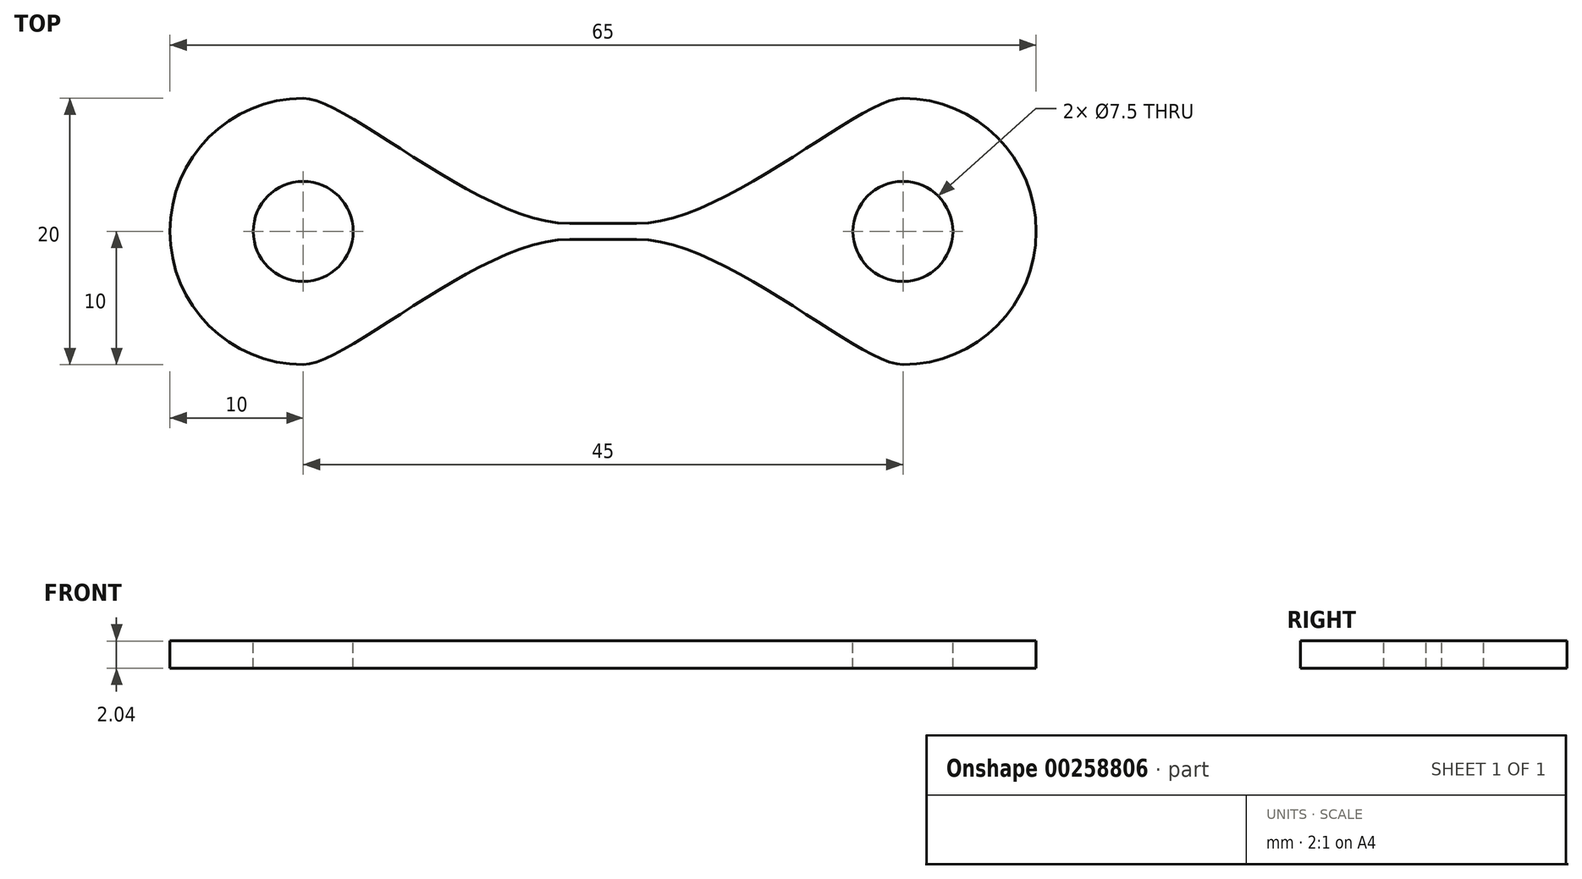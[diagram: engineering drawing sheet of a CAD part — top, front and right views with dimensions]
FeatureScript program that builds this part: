
annotation { "Feature Type Name" : "Feature", "Feature Type Description" : "" }
export const myFeature = defineFeature(function(context is Context, id is Id, definition is map)
    precondition{}
    {
        {
            var Q0;
            Q0=qCreatedBy(makeId("Right.planeOp"),FACE);
            var sketch = newSketch(context, id + "F0", { "sketchPlane" : qUnion([Q0])});
            skLineSegment(sketch, "E0.bottom", {"start": v(0.59, -1.02) * mm, "end": v(-0.59, -1.02) * mm});
            skLineSegment(sketch, "E0.top", {"start": v(0.59, 1.02) * mm, "end": v(-0.59, 1.02) * mm});
            skLineSegment(sketch, "E0.left", {"start": v(0.59, -1.02) * mm, "end": v(0.59, 1.02) * mm});
            skLineSegment(sketch, "E0.right", {"start": v(-0.59, -1.02) * mm, "end": v(-0.59, 1.02) * mm});
            skPoint(sketch, "E0.middle", {"position": v(0, 0) * mm});
            skSolve(sketch);
        }
        {
            var Q0;
            Q0=makeQuery(id+"F0.imprint","IMPRINT",FACE,{"disambiguationData":[TD([[makeQuery(id+"F0.imprint","IMPRINT",EDGE,{"derivedFrom":sQuery(id+"F0.wireOp",EDGE,"E0.bottom")}),-1.0]])]});
            extrude(context, id + "F1", {"entities" : qUnion([Q0]), "depth" : 2.5 * mm});
        }
        {
            var Q0;
            Q0=makeQuery(id+"F1.opExtrude","CAP_FACE",FACE,{"disambiguationData":[OSD([sQuery(id+"F0.wireOp",EDGE,"E0.bottom"),sQuery(id+"F0.wireOp",EDGE,"E0.top"),sQuery(id+"F0.wireOp",EDGE,"E0.left"),sQuery(id+"F0.wireOp",EDGE,"E0.right")])],"isStart":false});
            cPlane(context, id + "F2", {"entities" : qUnion([Q0]), "cplaneType" : CPlaneType.OFFSET, "offset" : 20 * mm, "width" : 150 * mm, "height" : 150 * mm});
        }
        {
            var Q0;
            Q0=qCreatedBy(id+"F2.planeOp",FACE);
            var sketch = newSketch(context, id + "F3", { "sketchPlane" : qUnion([Q0])});
            skLineSegment(sketch, "E1.bottom", {"start": v(10, -1.02) * mm, "end": v(-10, -1.02) * mm});
            skLineSegment(sketch, "E1.top", {"start": v(10, 1.02) * mm, "end": v(-10, 1.02) * mm});
            skLineSegment(sketch, "E1.left", {"start": v(10, -1.02) * mm, "end": v(10, 1.02) * mm});
            skLineSegment(sketch, "E1.right", {"start": v(-10, -1.02) * mm, "end": v(-10, 1.02) * mm});
            skPoint(sketch, "E1.middle", {"position": v(0, 0) * mm});
            skSolve(sketch);
        }
        {
            var Q1;
            Q1=makeQuery(id+"F1.opExtrude","CAP_FACE",FACE,{"disambiguationData":[OSD([sQuery(id+"F0.wireOp",EDGE,"E0.bottom"),sQuery(id+"F0.wireOp",EDGE,"E0.top"),sQuery(id+"F0.wireOp",EDGE,"E0.left"),sQuery(id+"F0.wireOp",EDGE,"E0.right")])],"isStart":false});
            var Q2;
            Q2=makeQuery(id+"F3.imprint","IMPRINT",FACE,{"disambiguationData":[TD([[makeQuery(id+"F3.imprint","IMPRINT",EDGE,{"derivedFrom":sQuery(id+"F3.wireOp",EDGE,"E1.bottom")}),-1.0]])]});
            loft(context, id + "F4", {"operationType" : NewBodyOperationType.ADD, "startCondition" : LoftEndDerivativeType.NORMAL_TO_PROFILE, "startMagnitude" : 1, "endCondition" : LoftEndDerivativeType.NORMAL_TO_PROFILE, "endMagnitude" : 0.5, "sheetProfilesArray" : [{ "sheetProfileEntities" : qUnion([Q1]) }, { "sheetProfileEntities" : qUnion([Q2]) }]});
        }
        {
            var Q0;
            Q0=qCreatedBy(makeId("Top.planeOp"),FACE);
            var sketch = newSketch(context, id + "F5", { "sketchPlane" : qUnion([Q0])});
            skArc(sketch, "E2", {"start": v(22.5, 10) * mm, "mid": v(32.5, 0) * mm, "end": v(22.5, -10) * mm});
            skLineSegment(sketch, "E3", {"start": v(22.5, 10) * mm, "end": v(22.5, -10) * mm});
            skSolve(sketch);
        }
        {
            var Q0;
            Q0 = qSketchRegion(id + "F5", true);
            var Q1;
            {var subQ0=sQuery(id+"F0.wireOp",EDGE,"E0.top");Q1=makeQuery(id+"F4.boolean.opBoolean","MERGE",FACE,{"derivedFrom":[makeQuery(id+"F1.opExtrude","SWEPT_FACE",FACE,{"disambiguationData":[OSD([subQ0])]}),makeQuery(id+"F4.opLoft","SWEPT_FACE",FACE,{"disambiguationData":[OSD([subQ0,sQuery(id+"F0.wireOp",EDGE,"E0.left"),sQuery(id+"F0.wireOp",EDGE,"E0.right"),sQuery(id+"F3.wireOp",EDGE,"E1.top"),sQuery(id+"F3.wireOp",EDGE,"E1.left"),sQuery(id+"F3.wireOp",EDGE,"E1.right")])]})]});}
            var Q2;
            {var subQ0=sQuery(id+"F0.wireOp",EDGE,"E0.bottom");Q2=makeQuery(id+"F4.boolean.opBoolean","MERGE",FACE,{"derivedFrom":[makeQuery(id+"F1.opExtrude","SWEPT_FACE",FACE,{"disambiguationData":[OSD([subQ0])]}),makeQuery(id+"F4.opLoft","SWEPT_FACE",FACE,{"disambiguationData":[OSD([subQ0,sQuery(id+"F0.wireOp",EDGE,"E0.left"),sQuery(id+"F0.wireOp",EDGE,"E0.right"),sQuery(id+"F3.wireOp",EDGE,"E1.bottom"),sQuery(id+"F3.wireOp",EDGE,"E1.left"),sQuery(id+"F3.wireOp",EDGE,"E1.right")])]})]});}
            extrude(context, id + "F6", {"entities" : qUnion([Q0]), "operationType" : NewBodyOperationType.ADD, "endBound" : BoundingType.UP_TO_SURFACE, "endBoundEntityFace" : qUnion([Q1]), "depth" : 25 * mm, "hasSecondDirection" : true, "secondDirectionBound" : SecondDirectionBoundingType.UP_TO_SURFACE, "secondDirectionOppositeDirection" : true, "secondDirectionBoundEntityFace" : qUnion([Q2]), "secondDirectionDepth" : 25 * mm});
        }
        {
            var Q0;
            {var subQ0=sQuery(id+"F0.wireOp",EDGE,"E0.top");Q0=makeQuery(id+"F6.boolean.opBoolean","MERGE",FACE,{"derivedFrom":[makeQuery(id+"F4.boolean.opBoolean","MERGE",FACE,{"derivedFrom":[makeQuery(id+"F1.opExtrude","SWEPT_FACE",FACE,{"disambiguationData":[OSD([subQ0])]}),makeQuery(id+"F4.opLoft","SWEPT_FACE",FACE,{"disambiguationData":[OSD([subQ0,sQuery(id+"F0.wireOp",EDGE,"E0.left"),sQuery(id+"F0.wireOp",EDGE,"E0.right"),sQuery(id+"F3.wireOp",EDGE,"E1.top"),sQuery(id+"F3.wireOp",EDGE,"E1.left"),sQuery(id+"F3.wireOp",EDGE,"E1.right")])]})]}),makeQuery(id+"F6.opExtrude","CAP_FACE",FACE,{"disambiguationData":[OSD([sQuery(id+"F5.wireOp",EDGE,"E2"),sQuery(id+"F5.wireOp",EDGE,"E3")])],"isStart":false})]});}
            var sketch = newSketch(context, id + "F7", { "sketchPlane" : qUnion([Q0])});
            skCircle(sketch, "E4", {"center": v(22.5, 0) * mm, "radius": 3.75 * mm});
            skSolve(sketch);
        }
        {
            var Q0;
            Q0=makeQuery(id+"F7.imprint","IMPRINT",FACE,{"disambiguationData":[TD([[makeQuery(id+"F7.imprint","IMPRINT",EDGE,{"derivedFrom":sQuery(id+"F7.wireOp",EDGE,"E4")}),1.0]])]});
            extrude(context, id + "F8", {"entities" : qUnion([Q0]), "operationType" : NewBodyOperationType.REMOVE, "endBound" : BoundingType.UP_TO_NEXT, "oppositeDirection" : true, "depth" : 25 * mm});
        }
        {
            var Q0;
            Q0=makeQuery(id+"F1.opExtrude","SWEPT_BODY",BODY,{"disambiguationData":[OSD([sQuery(id+"F0.wireOp",EDGE,"E0.bottom"),sQuery(id+"F0.wireOp",EDGE,"E0.top"),sQuery(id+"F0.wireOp",EDGE,"E0.left"),sQuery(id+"F0.wireOp",EDGE,"E0.right")])]});
            var Q1;
            Q1=makeQuery(id+"F1.opExtrude","CAP_FACE",FACE,{"disambiguationData":[OSD([sQuery(id+"F0.wireOp",EDGE,"E0.bottom"),sQuery(id+"F0.wireOp",EDGE,"E0.top"),sQuery(id+"F0.wireOp",EDGE,"E0.left"),sQuery(id+"F0.wireOp",EDGE,"E0.right")])],"isStart":true});
            mirror(context, id + "F9", {"operationType" : NewBodyOperationType.ADD, "entities" : qUnion([Q0]), "mirrorPlane" : qUnion([Q1])});
        }
    });
